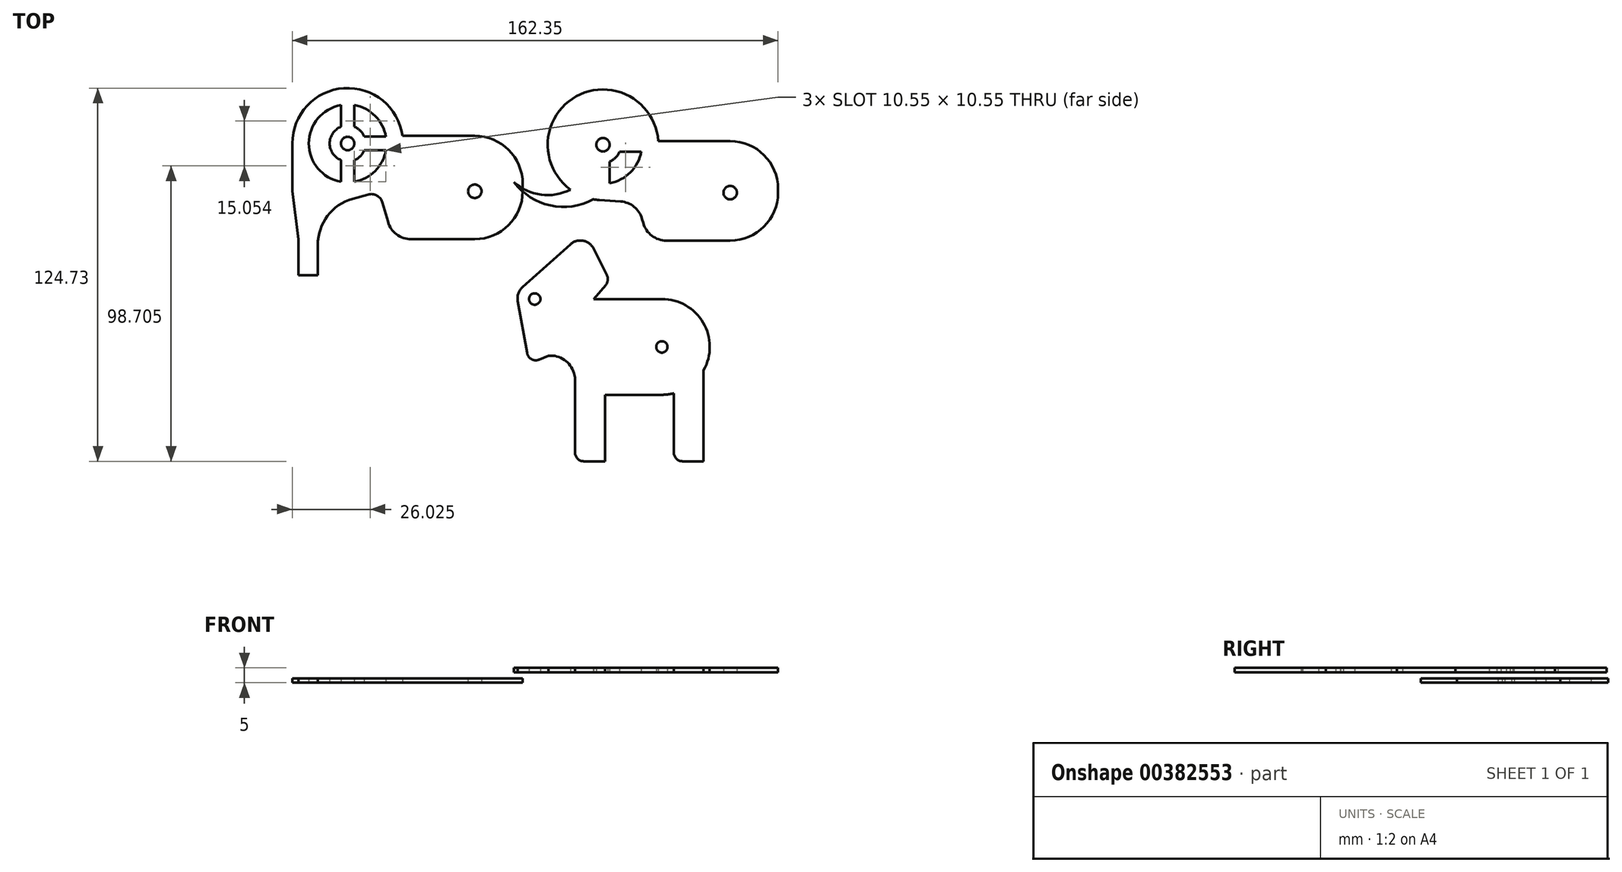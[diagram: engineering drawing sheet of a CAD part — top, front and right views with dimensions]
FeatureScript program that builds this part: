
annotation { "Feature Type Name" : "Feature", "Feature Type Description" : "" }
export const myFeature = defineFeature(function(context is Context, id is Id, definition is map)
    precondition{}
    {
        {
            var Q0;
            Q0=qCreatedBy(makeId("Top.planeOp"),FACE);
            cPlane(context, id + "F0", {"entities" : qUnion([Q0]), "cplaneType" : CPlaneType.OFFSET, "offset" : 3.5 * mm, "width" : 150 * mm, "height" : 150 * mm});
        }
        {
            var Q0;
            Q0=qCreatedBy(makeId("Top.planeOp"),FACE);
            var sketch = newSketch(context, id + "F1", { "sketchPlane" : qUnion([Q0])});
            skLineSegment(sketch, "E0", {"start": v(-0.32, 16.22) * mm, "end": v(23.85, 16.22) * mm});
            skLineSegment(sketch, "E1", {"start": v(23.85, 16.22) * mm, "end": v(23.85, 0.22) * mm, "construction": true});
            skArc(sketch, "E2", {"start": v(39.85, 0.22) * mm, "mid": v(35.16, 11.54) * mm, "end": v(23.85, 16.22) * mm});
            skArc(sketch, "E3", {"start": v(23.85, -18.28) * mm, "mid": v(35.16, -13.6) * mm, "end": v(39.85, -2.28) * mm});
            skLineSegment(sketch, "E4", {"start": v(23.85, -18.28) * mm, "end": v(2.5, -18.28) * mm});
            skLineSegment(sketch, "E5", {"start": v(-5.2, -12.45) * mm, "end": v(-6.98, -6.13) * mm});
            skLineSegment(sketch, "E6", {"start": v(-11.91, -3.36) * mm, "end": v(-16.98, -4.8) * mm});
            skLineSegment(sketch, "E7", {"start": v(-28.64, -20.2) * mm, "end": v(-28.64, -30.28) * mm});
            skLineSegment(sketch, "E8", {"start": v(-28.64, -30.28) * mm, "end": v(-35.14, -30.28) * mm});
            skLineSegment(sketch, "E9", {"start": v(-35.14, -30.28) * mm, "end": v(-35.14, -18.28) * mm});
            skLineSegment(sketch, "E10", {"start": v(-37.15, -2.28) * mm, "end": v(-35.14, -18.28) * mm});
            skLineSegment(sketch, "E11", {"start": v(39.85, 0.22) * mm, "end": v(39.85, -2.28) * mm});
            skPoint(sketch, "E12.visualSharp", {"position": v(-28.64, -8.08) * mm});
            skArc(sketch, "E12.filletArc", {"start": v(-16.98, -4.8) * mm, "mid": v(-25.4, -10.53) * mm, "end": v(-28.64, -20.2) * mm});
            skPoint(sketch, "E13.visualSharp", {"position": v(-8.06, -2.28) * mm});
            skArc(sketch, "E13.filletArc", {"start": v(-6.98, -6.13) * mm, "mid": v(-8.87, -3.72) * mm, "end": v(-11.91, -3.36) * mm});
            skPoint(sketch, "E14.visualSharp", {"position": v(-3.55, -18.28) * mm});
            skArc(sketch, "E14.filletArc", {"start": v(-5.2, -12.45) * mm, "mid": v(-2.32, -16.66) * mm, "end": v(2.5, -18.28) * mm});
            skArc(sketch, "E15", {"start": v(-0.32, 16.22) * mm, "mid": v(-19.9, 32.18) * mm, "end": v(-37.15, 13.72) * mm});
            skLineSegment(sketch, "E16", {"start": v(-37.15, 13.72) * mm, "end": v(-37.15, -2.28) * mm});
            skCircle(sketch, "E17", {"center": v(-18.65, 13.72) * mm, "radius": 2.25 * mm});
            skCircle(sketch, "E18", {"center": v(23.85, -2.28) * mm, "radius": 2.25 * mm});
            skArc(sketch, "E19", {"start": v(-20.9, 19.28) * mm, "mid": v(-24.65, 13.72) * mm, "end": v(-20.9, 8.16) * mm});
            skArc(sketch, "E20", {"start": v(-20.9, 26.53) * mm, "mid": v(-31.65, 13.72) * mm, "end": v(-20.9, 0.92) * mm});
            skLineSegment(sketch, "E21", {"start": v(-13.09, 11.47) * mm, "end": v(-5.85, 11.47) * mm});
            skLineSegment(sketch, "E22", {"start": v(-20.9, 8.16) * mm, "end": v(-20.9, 0.92) * mm});
            skLineSegment(sketch, "E23", {"start": v(-16.4, 8.16) * mm, "end": v(-16.4, 0.92) * mm});
            skLineSegment(sketch, "E24", {"start": v(-20.9, 19.28) * mm, "end": v(-20.9, 26.53) * mm});
            skPoint(sketch, "E25.orphan", {"position": v(-20.9, 13.72) * mm});
            skLineSegment(sketch, "E26.trimOffspring", {"start": v(-16.4, 19.28) * mm, "end": v(-16.4, 26.53) * mm});
            skLineSegment(sketch, "E27.trimOffspring", {"start": v(-13.09, 15.97) * mm, "end": v(-5.85, 15.97) * mm});
            skPoint(sketch, "E28.orphan", {"position": v(-20.9, 28.34) * mm});
            skPoint(sketch, "E29.orphan", {"position": v(-16.4, 28.34) * mm});
            skPoint(sketch, "E30.start.orphan", {"position": v(-18.65, 15.97) * mm});
            skPoint(sketch, "E31.orphan", {"position": v(-16.4, 13.72) * mm});
            skPoint(sketch, "E32.orphan", {"position": v(-18.65, 11.47) * mm});
            skPoint(sketch, "E33.orphan", {"position": v(-16.4, -1.16) * mm});
            skPoint(sketch, "E34.orphan", {"position": v(-20.9, -1.16) * mm});
            skArc(sketch, "E35.trimOffspring", {"start": v(-16.4, 0.92) * mm, "mid": v(-9.46, 4.53) * mm, "end": v(-5.85, 11.47) * mm});
            skArc(sketch, "E36.trimOffspring", {"start": v(-16.4, 8.16) * mm, "mid": v(-14.4, 9.48) * mm, "end": v(-13.09, 11.47) * mm});
            skArc(sketch, "E37.trimOffspring", {"start": v(-13.09, 15.97) * mm, "mid": v(-14.4, 17.96) * mm, "end": v(-16.4, 19.28) * mm});
            skArc(sketch, "E38.trimOffspring", {"start": v(-5.85, 15.97) * mm, "mid": v(-9.46, 22.91) * mm, "end": v(-16.4, 26.53) * mm});
            skPoint(sketch, "E39.orphan", {"position": v(-4.26, 15.97) * mm});
            skPoint(sketch, "E40.orphan", {"position": v(-4.26, 11.47) * mm});
            skSolve(sketch);
        }
        {
            var Q0;
            Q0=makeQuery(id+"F1.imprint","IMPRINT",FACE,{"disambiguationData":[TD([[makeQuery(id+"F1.imprint","IMPRINT",EDGE,{"derivedFrom":sQuery(id+"F1.wireOp",EDGE,"ZgbVZM7l-9nBI-ljWO-ztFK-aUv2txpj9Slg")}),1.0]])]});
            var Q1;
            Q1=makeQuery(id+"F1.imprint","IMPRINT",FACE,{"disambiguationData":[TD([[makeQuery(id+"F1.imprint","IMPRINT",EDGE,{"derivedFrom":sQuery(id+"F1.wireOp",EDGE,"xAUIcYyB-5KoE-Dqfu-aYJm-RxGYsceZYXx7")}),1.0]])]});
            var Q2;
            Q2=makeQuery(id+"F1.imprint","IMPRINT",FACE,{"disambiguationData":[TD([[makeQuery(id+"F1.imprint","IMPRINT",EDGE,{"derivedFrom":sQuery(id+"F1.wireOp",EDGE,"E0")}),-1.0]])]});
            extrude(context, id + "F2", {"entities" : qUnion([Q0, Q1, Q2]), "depth" : 1.5 * mm});
        }
        {
            var Q0;
            Q0=qCreatedBy(id+"F0.planeOp",FACE);
            var sketch = newSketch(context, id + "F3", { "sketchPlane" : qUnion([Q0])});
            skLineSegment(sketch, "E41", {"start": v(85.16, 14.51) * mm, "end": v(109.2, 14.51) * mm});
            skLineSegment(sketch, "E42", {"start": v(109.2, 14.51) * mm, "end": v(109.2, -1.49) * mm, "construction": true});
            skArc(sketch, "E43", {"start": v(125.2, -1.49) * mm, "mid": v(120.51, 9.82) * mm, "end": v(109.2, 14.51) * mm});
            skArc(sketch, "E44", {"start": v(109.2, -18.74) * mm, "mid": v(120.51, -14.05) * mm, "end": v(125.2, -2.74) * mm});
            skLineSegment(sketch, "E45", {"start": v(109.2, -18.74) * mm, "end": v(87.86, -18.74) * mm});
            skLineSegment(sketch, "E46", {"start": v(80.16, -12.9) * mm, "end": v(79.76, -11.48) * mm});
            skLineSegment(sketch, "E47", {"start": v(125.2, -1.49) * mm, "end": v(125.2, -2.74) * mm});
            skPoint(sketch, "E48.visualSharp", {"position": v(81.8, -18.74) * mm});
            skArc(sketch, "E48.filletArc", {"start": v(80.16, -12.9) * mm, "mid": v(83.03, -17.12) * mm, "end": v(87.86, -18.74) * mm});
            skCircle(sketch, "E49", {"center": v(66.7, 13.26) * mm, "radius": 18.5 * mm});
            skLineSegment(sketch, "E50", {"start": v(72.59, -5.67) * mm, "end": v(65.47, -5.2) * mm});
            skPoint(sketch, "E51.visualSharp", {"position": v(78.22, -6.05) * mm});
            skArc(sketch, "E51.filletArc", {"start": v(79.76, -11.48) * mm, "mid": v(77.1, -7.44) * mm, "end": v(72.59, -5.67) * mm});
            skArc(sketch, "E52", {"start": v(36.94, 0.8) * mm, "mid": v(46, -3.4) * mm, "end": v(55.83, -1.7) * mm});
            skArc(sketch, "E53", {"start": v(36.94, 0.8) * mm, "mid": v(49.12, -7.01) * mm, "end": v(63.44, -4.95) * mm});
            skCircle(sketch, "E54", {"center": v(66.7, 13.26) * mm, "radius": 2.25 * mm});
            skCircle(sketch, "E55", {"center": v(109.2, -2.74) * mm, "radius": 2.25 * mm});
            skArc(sketch, "E56", {"start": v(68.95, 7.7) * mm, "mid": v(70.94, 9.02) * mm, "end": v(72.26, 11.01) * mm});
            skArc(sketch, "E57", {"start": v(68.95, 0.46) * mm, "mid": v(75.9, 4.07) * mm, "end": v(79.5, 11.01) * mm});
            skLineSegment(sketch, "E58.trimOffspring", {"start": v(72.26, 11.01) * mm, "end": v(79.5, 11.01) * mm});
            skLineSegment(sketch, "E59.trimOffspring", {"start": v(68.95, 7.7) * mm, "end": v(68.95, 0.46) * mm});
            skPoint(sketch, "E60.start.orphan", {"position": v(66.7, 11.01) * mm});
            skPoint(sketch, "E61.start.orphan", {"position": v(68.95, 13.26) * mm});
            skPoint(sketch, "E62.orphan", {"position": v(64.45, 13.26) * mm});
            skPoint(sketch, "E63.orphan", {"position": v(66.7, 15.51) * mm});
            skPoint(sketch, "E64.end.orphan", {"position": v(64.95, -0.42) * mm});
            skPoint(sketch, "E65.orphan", {"position": v(68.95, -0.42) * mm});
            skPoint(sketch, "E66.orphan", {"position": v(80.43, 11.01) * mm});
            skPoint(sketch, "E67.end.orphan", {"position": v(80.43, 15.01) * mm});
            skSolve(sketch);
        }
        {
            var Q0;
            Q0 = qSketchRegion(id + "F3", true);
            extrude(context, id + "F4", {"entities" : qUnion([Q0]), "depth" : 1.5 * mm});
        }
        {
            var Q0;
            Q0=qCreatedBy(id+"F0.planeOp",FACE);
            var sketch = newSketch(context, id + "F5", { "sketchPlane" : qUnion([Q0])});
            skLineSegment(sketch, "E68", {"start": v(63.64, -38.28) * mm, "end": v(86.37, -38.28) * mm});
            skLineSegment(sketch, "E69", {"start": v(86.37, -38.28) * mm, "end": v(86.37, -54.28) * mm, "construction": true});
            skArc(sketch, "E70", {"start": v(102.37, -54.28) * mm, "mid": v(97.69, -42.97) * mm, "end": v(86.37, -38.28) * mm});
            skArc(sketch, "E71", {"start": v(86.37, -70.28) * mm, "mid": v(97.69, -65.6) * mm, "end": v(102.37, -54.28) * mm});
            skLineSegment(sketch, "E72", {"start": v(86.37, -70.28) * mm, "end": v(65.03, -70.28) * mm});
            skLineSegment(sketch, "E73", {"start": v(57.33, -64.45) * mm, "end": v(56.93, -63.03) * mm});
            skLineSegment(sketch, "E74", {"start": v(102.37, -54.28) * mm, "end": v(102.37, -54.28) * mm});
            skPoint(sketch, "E75.visualSharp", {"position": v(58.97, -70.28) * mm});
            skArc(sketch, "E75.filletArc", {"start": v(57.33, -64.45) * mm, "mid": v(60.2, -68.66) * mm, "end": v(65.03, -70.28) * mm});
            skPoint(sketch, "E76.visualSharp", {"position": v(55.12, -56.61) * mm});
            skArc(sketch, "E76.filletArc", {"start": v(56.93, -63.03) * mm, "mid": v(53.75, -58.6) * mm, "end": v(48.48, -57.23) * mm});
            skCircle(sketch, "E77", {"center": v(86.37, -54.28) * mm, "radius": 1.9 * mm});
            skLineSegment(sketch, "E78", {"start": v(63.64, -38.28) * mm, "end": v(67.6, -33.57) * mm});
            skLineSegment(sketch, "E79", {"start": v(67.98, -30.3) * mm, "end": v(63.6, -21.5) * mm});
            skLineSegment(sketch, "E80", {"start": v(55.8, -20) * mm, "end": v(39.78, -34.3) * mm});
            skLineSegment(sketch, "E81", {"start": v(38.2, -38.9) * mm, "end": v(41.3, -56.28) * mm});
            skPoint(sketch, "E82.center.orphan", {"position": v(43.87, -38.28) * mm});
            skLineSegment(sketch, "E83", {"start": v(48.48, -57.23) * mm, "end": v(45.41, -58.52) * mm});
            skLineSegment(sketch, "E84", {"start": v(57.33, -64.45) * mm, "end": v(57.33, -89.51) * mm});
            skLineSegment(sketch, "E85", {"start": v(60.33, -92.51) * mm, "end": v(67.33, -92.51) * mm});
            skLineSegment(sketch, "E86", {"start": v(67.33, -92.51) * mm, "end": v(67.33, -67.2) * mm});
            skLineSegment(sketch, "E87", {"start": v(67.33, -67.2) * mm, "end": v(90.33, -67.2) * mm, "construction": true});
            skLineSegment(sketch, "E88", {"start": v(90.33, -67.2) * mm, "end": v(90.33, -89.51) * mm});
            skLineSegment(sketch, "E89", {"start": v(93.33, -92.51) * mm, "end": v(100.33, -92.51) * mm});
            skLineSegment(sketch, "E90", {"start": v(100.33, -92.51) * mm, "end": v(100.33, -62.1) * mm});
            skPoint(sketch, "E91.visualSharp", {"position": v(68.86, -32.07) * mm});
            skArc(sketch, "E91.filletArc", {"start": v(67.6, -33.57) * mm, "mid": v(68.28, -32) * mm, "end": v(67.98, -30.3) * mm});
            skPoint(sketch, "E92.visualSharp", {"position": v(60.68, -15.62) * mm});
            skArc(sketch, "E92.filletArc", {"start": v(63.6, -21.5) * mm, "mid": v(60.07, -18.8) * mm, "end": v(55.8, -20) * mm});
            skPoint(sketch, "E93.visualSharp", {"position": v(37.7, -36.16) * mm});
            skArc(sketch, "E93.filletArc", {"start": v(39.78, -34.3) * mm, "mid": v(38.4, -36.4) * mm, "end": v(38.2, -38.9) * mm});
            skPoint(sketch, "E94.visualSharp", {"position": v(41.96, -59.97) * mm});
            skArc(sketch, "E94.filletArc", {"start": v(41.3, -56.28) * mm, "mid": v(42.82, -58.39) * mm, "end": v(45.41, -58.52) * mm});
            skCircle(sketch, "E95", {"center": v(43.87, -38.28) * mm, "radius": 1.9 * mm});
            skPoint(sketch, "E96.visualSharp", {"position": v(57.33, -92.51) * mm});
            skArc(sketch, "E96.filletArc", {"start": v(57.33, -89.51) * mm, "mid": v(58.2, -91.63) * mm, "end": v(60.33, -92.51) * mm});
            skPoint(sketch, "E97.visualSharp", {"position": v(90.33, -92.51) * mm});
            skArc(sketch, "E97.filletArc", {"start": v(90.33, -89.51) * mm, "mid": v(91.2, -91.63) * mm, "end": v(93.33, -92.51) * mm});
            skSolve(sketch);
        }
        {
            var Q0;
            Q0 = qSketchRegion(id + "F5", true);
            extrude(context, id + "F6", {"entities" : qUnion([Q0]), "depth" : 1.5 * mm});
        }
    });
